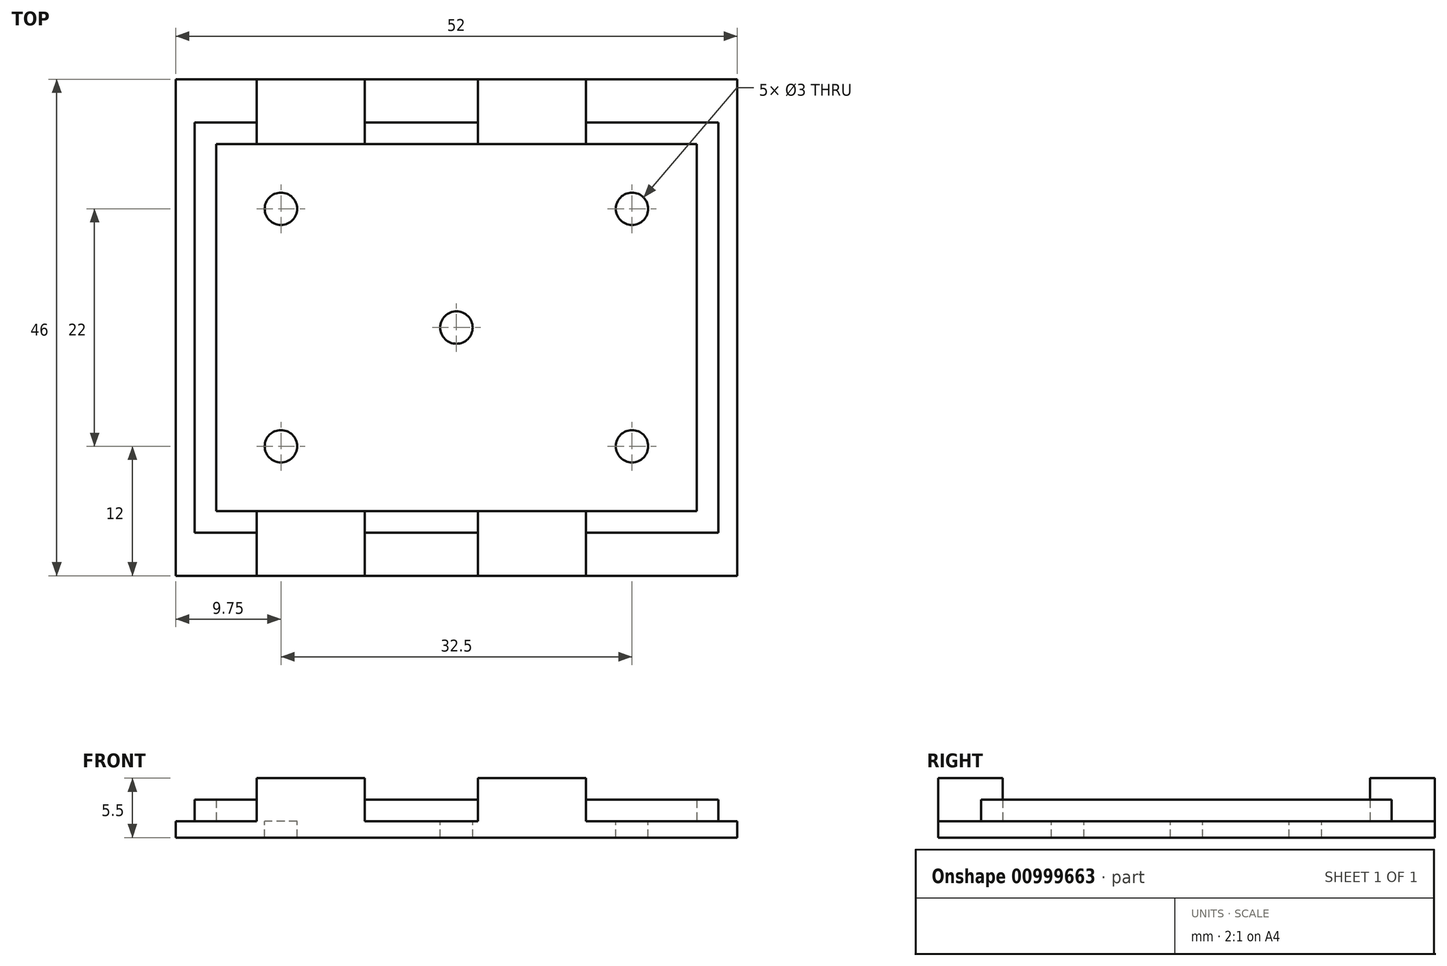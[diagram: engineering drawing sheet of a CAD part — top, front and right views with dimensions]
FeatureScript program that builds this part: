
annotation { "Feature Type Name" : "Feature", "Feature Type Description" : "" }
export const myFeature = defineFeature(function(context is Context, id is Id, definition is map)
    precondition{}
    {
        {
            var Q0;
            Q0=qCreatedBy(makeId("Top.planeOp"),FACE);
            var sketch = newSketch(context, id + "F0", { "sketchPlane" : qUnion([Q0])});
            skLineSegment(sketch, "E0.bottom", {"start": v(0, 0) * mm, "end": v(52, 0) * mm});
            skLineSegment(sketch, "E0.top", {"start": v(0, -46) * mm, "end": v(52, -46) * mm});
            skLineSegment(sketch, "E0.left", {"start": v(0, 0) * mm, "end": v(0, -46) * mm});
            skLineSegment(sketch, "E0.right", {"start": v(52, 0) * mm, "end": v(52, -46) * mm});
            skSolve(sketch);
        }
        {
            var Q0;
            Q0 = qSketchRegion(id + "F0", true);
            extrude(context, id + "F1", {"entities" : qUnion([Q0]), "depth" : 1.5 * mm, "offsetDistance" : 25 * mm});
        }
        {
            var Q0;
            Q0=makeQuery(id+"F1.opExtrude","CAP_FACE",FACE,{"disambiguationData":[OSD([sQuery(id+"F0.wireOp",EDGE,"E0.bottom"),sQuery(id+"F0.wireOp",EDGE,"E0.top"),sQuery(id+"F0.wireOp",EDGE,"E0.left"),sQuery(id+"F0.wireOp",EDGE,"E0.right")])],"isStart":false});
            var sketch = newSketch(context, id + "F2", { "sketchPlane" : qUnion([Q0])});
            skLineSegment(sketch, "E1.bottom", {"start": v(3.75, -6) * mm, "end": v(48.25, -6) * mm});
            skLineSegment(sketch, "E1.top", {"start": v(3.75, -40) * mm, "end": v(48.25, -40) * mm});
            skLineSegment(sketch, "E1.left", {"start": v(3.75, -6) * mm, "end": v(3.75, -40) * mm});
            skLineSegment(sketch, "E1.right", {"start": v(48.25, -6) * mm, "end": v(48.25, -40) * mm});
            skLineSegment(sketch, "E2.bottom", {"start": v(1.75, -4) * mm, "end": v(50.25, -4) * mm});
            skLineSegment(sketch, "E2.top", {"start": v(1.75, -42) * mm, "end": v(50.25, -42) * mm});
            skLineSegment(sketch, "E2.left", {"start": v(1.75, -4) * mm, "end": v(1.75, -42) * mm});
            skLineSegment(sketch, "E2.right", {"start": v(50.25, -4) * mm, "end": v(50.25, -42) * mm});
            skSolve(sketch);
        }
        {
            var Q0;
            Q0 = qSketchRegion(id + "F2", true);
            extrude(context, id + "F3", {"entities" : qUnion([Q0]), "operationType" : NewBodyOperationType.ADD, "depth" : 2 * mm, "offsetDistance" : 25 * mm});
        }
        {
            var Q0;
            {var subQ0=sQuery(id+"F0.wireOp",EDGE,"E0.left");var subQ1=sQuery(id+"F0.wireOp",EDGE,"E0.top");var subQ2=sQuery(id+"F0.wireOp",EDGE,"E0.right");var subQ3=sQuery(id+"F0.wireOp",EDGE,"E0.bottom");Q0=makeQuery(id+"F3.boolean.opBoolean","SPLIT",FACE,{"disambiguationData":[TD([makeQuery(id+"F1.opExtrude","SWEPT_FACE",FACE,{"disambiguationData":[OSD([subQ3])]})])],"derivedFrom":makeQuery(id+"F1.opExtrude","CAP_FACE",FACE,{"disambiguationData":[OSD([subQ3,subQ1,subQ0,subQ2])],"isStart":false})});}
            var sketch = newSketch(context, id + "F4", { "sketchPlane" : qUnion([Q0])});
            skLineSegment(sketch, "E3.bottom", {"start": v(17.5, -46) * mm, "end": v(7.5, -46) * mm});
            skLineSegment(sketch, "E3.top", {"start": v(17.5, -42) * mm, "end": v(7.5, -42) * mm});
            skLineSegment(sketch, "E3.left", {"start": v(17.5, -46) * mm, "end": v(17.5, -42) * mm});
            skLineSegment(sketch, "E3.right", {"start": v(7.5, -46) * mm, "end": v(7.5, -42) * mm});
            skLineSegment(sketch, "E4.bottom", {"start": v(28, -46) * mm, "end": v(38, -46) * mm});
            skLineSegment(sketch, "E4.top", {"start": v(28, -42) * mm, "end": v(38, -42) * mm});
            skLineSegment(sketch, "E4.left", {"start": v(28, -46) * mm, "end": v(28, -42) * mm});
            skLineSegment(sketch, "E4.right", {"start": v(38, -46) * mm, "end": v(38, -42) * mm});
            skLineSegment(sketch, "E5.bottom", {"start": v(28, 0) * mm, "end": v(38, 0) * mm});
            skLineSegment(sketch, "E5.top", {"start": v(28, -4) * mm, "end": v(38, -4) * mm});
            skLineSegment(sketch, "E5.left", {"start": v(28, 0) * mm, "end": v(28, -4) * mm});
            skLineSegment(sketch, "E5.right", {"start": v(38, 0) * mm, "end": v(38, -4) * mm});
            skLineSegment(sketch, "E6.bottom", {"start": v(7.5, 0) * mm, "end": v(17.5, 0) * mm});
            skLineSegment(sketch, "E6.top", {"start": v(7.5, -4) * mm, "end": v(17.5, -4) * mm});
            skLineSegment(sketch, "E6.left", {"start": v(7.5, 0) * mm, "end": v(7.5, -4) * mm});
            skLineSegment(sketch, "E6.right", {"start": v(17.5, 0) * mm, "end": v(17.5, -4) * mm});
            skSolve(sketch);
        }
        {
            var Q0;
            Q0 = qSketchRegion(id + "F4", true);
            extrude(context, id + "F5", {"entities" : qUnion([Q0]), "operationType" : NewBodyOperationType.ADD, "depth" : 4 * mm, "offsetDistance" : 25 * mm});
        }
        {
            var Q0;
            Q0=makeQuery(id+"F3.boolean.opBoolean","SPLIT",FACE,{"disambiguationData":[TD([makeQuery(id+"F3.opExtrude","SWEPT_FACE",FACE,{"disambiguationData":[OSD([sQuery(id+"F2.wireOp",EDGE,"E1.bottom")])]})])],"derivedFrom":makeQuery(id+"F1.opExtrude","CAP_FACE",FACE,{"disambiguationData":[OSD([sQuery(id+"F0.wireOp",EDGE,"E0.bottom"),sQuery(id+"F0.wireOp",EDGE,"E0.top"),sQuery(id+"F0.wireOp",EDGE,"E0.left"),sQuery(id+"F0.wireOp",EDGE,"E0.right")])],"isStart":false})});
            var sketch = newSketch(context, id + "F6", { "sketchPlane" : qUnion([Q0])});
            skCircle(sketch, "E7", {"center": v(9.75, -12) * mm, "radius": 1.5 * mm});
            skCircle(sketch, "E8", {"center": v(42.25, -12) * mm, "radius": 1.5 * mm});
            skCircle(sketch, "E9", {"center": v(26, -23) * mm, "radius": 1.5 * mm});
            skCircle(sketch, "E10", {"center": v(9.75, -34) * mm, "radius": 1.5 * mm});
            skCircle(sketch, "E11", {"center": v(42.25, -34) * mm, "radius": 1.5 * mm});
            skPoint(sketch, "E12", {"position": v(48.25, -23) * mm});
            skPoint(sketch, "E13", {"position": v(26, -6) * mm});
            skSolve(sketch);
        }
        {
            var Q0;
            Q0 = qSketchRegion(id + "F6", true);
            extrude(context, id + "F7", {"entities" : qUnion([Q0]), "operationType" : NewBodyOperationType.REMOVE, "oppositeDirection" : true, "depth" : 25 * mm, "offsetDistance" : 25 * mm});
        }
        {
            var Q0;
            Q0=makeQuery(id+"F5.opExtrude","SWEPT_FACE",FACE,{"disambiguationData":[OSD([sQuery(id+"F4.wireOp",EDGE,"E6.top")])]});
            var Q1;
            Q1=makeQuery(id+"F3.opExtrude","SWEPT_FACE",FACE,{"disambiguationData":[OSD([sQuery(id+"F2.wireOp",EDGE,"E1.bottom")])]});
            extrude(context, id + "F8", {"entities" : qUnion([Q0]), "operationType" : NewBodyOperationType.ADD, "endBound" : BoundingType.UP_TO_SURFACE, "depth" : 25 * mm, "endBoundEntityFace" : qUnion([Q1]), "offsetDistance" : 25 * mm});
        }
        {
            var Q0;
            Q0=makeQuery(id+"F5.opExtrude","SWEPT_FACE",FACE,{"disambiguationData":[OSD([sQuery(id+"F4.wireOp",EDGE,"E5.top")])]});
            var Q1;
            Q1=makeQuery(id+"F8.boolean.opBoolean","MERGE",FACE,{"derivedFrom":[makeQuery(id+"F3.opExtrude","SWEPT_FACE",FACE,{"disambiguationData":[OSD([sQuery(id+"F2.wireOp",EDGE,"E1.bottom")])]}),makeQuery(id+"F8.opExtrude","CAP_FACE",FACE,{"disambiguationData":[OSD([sQuery(id+"F4.wireOp",EDGE,"E6.top")])],"isStart":false})]});
            extrude(context, id + "F9", {"entities" : qUnion([Q0]), "operationType" : NewBodyOperationType.ADD, "endBound" : BoundingType.UP_TO_SURFACE, "depth" : 25 * mm, "endBoundEntityFace" : qUnion([Q1]), "offsetDistance" : 25 * mm});
        }
        {
            var Q0;
            Q0=makeQuery(id+"F5.opExtrude","SWEPT_FACE",FACE,{"disambiguationData":[OSD([sQuery(id+"F4.wireOp",EDGE,"E4.top")])]});
            var Q1;
            Q1=makeQuery(id+"F3.opExtrude","SWEPT_FACE",FACE,{"disambiguationData":[OSD([sQuery(id+"F2.wireOp",EDGE,"E1.top")])]});
            extrude(context, id + "F10", {"entities" : qUnion([Q0]), "operationType" : NewBodyOperationType.ADD, "endBound" : BoundingType.UP_TO_SURFACE, "depth" : 25 * mm, "endBoundEntityFace" : qUnion([Q1]), "offsetDistance" : 25 * mm});
        }
        {
            var Q0;
            Q0=makeQuery(id+"F5.opExtrude","SWEPT_FACE",FACE,{"disambiguationData":[OSD([sQuery(id+"F4.wireOp",EDGE,"E3.top")])]});
            var Q1;
            Q1=makeQuery(id+"F10.boolean.opBoolean","MERGE",FACE,{"derivedFrom":[makeQuery(id+"F3.opExtrude","SWEPT_FACE",FACE,{"disambiguationData":[OSD([sQuery(id+"F2.wireOp",EDGE,"E1.top")])]}),makeQuery(id+"F10.opExtrude","CAP_FACE",FACE,{"disambiguationData":[OSD([sQuery(id+"F4.wireOp",EDGE,"E4.top")])],"isStart":false})]});
            extrude(context, id + "F11", {"entities" : qUnion([Q0]), "operationType" : NewBodyOperationType.ADD, "endBound" : BoundingType.UP_TO_SURFACE, "depth" : 25 * mm, "endBoundEntityFace" : qUnion([Q1]), "offsetDistance" : 25 * mm});
        }
    });
